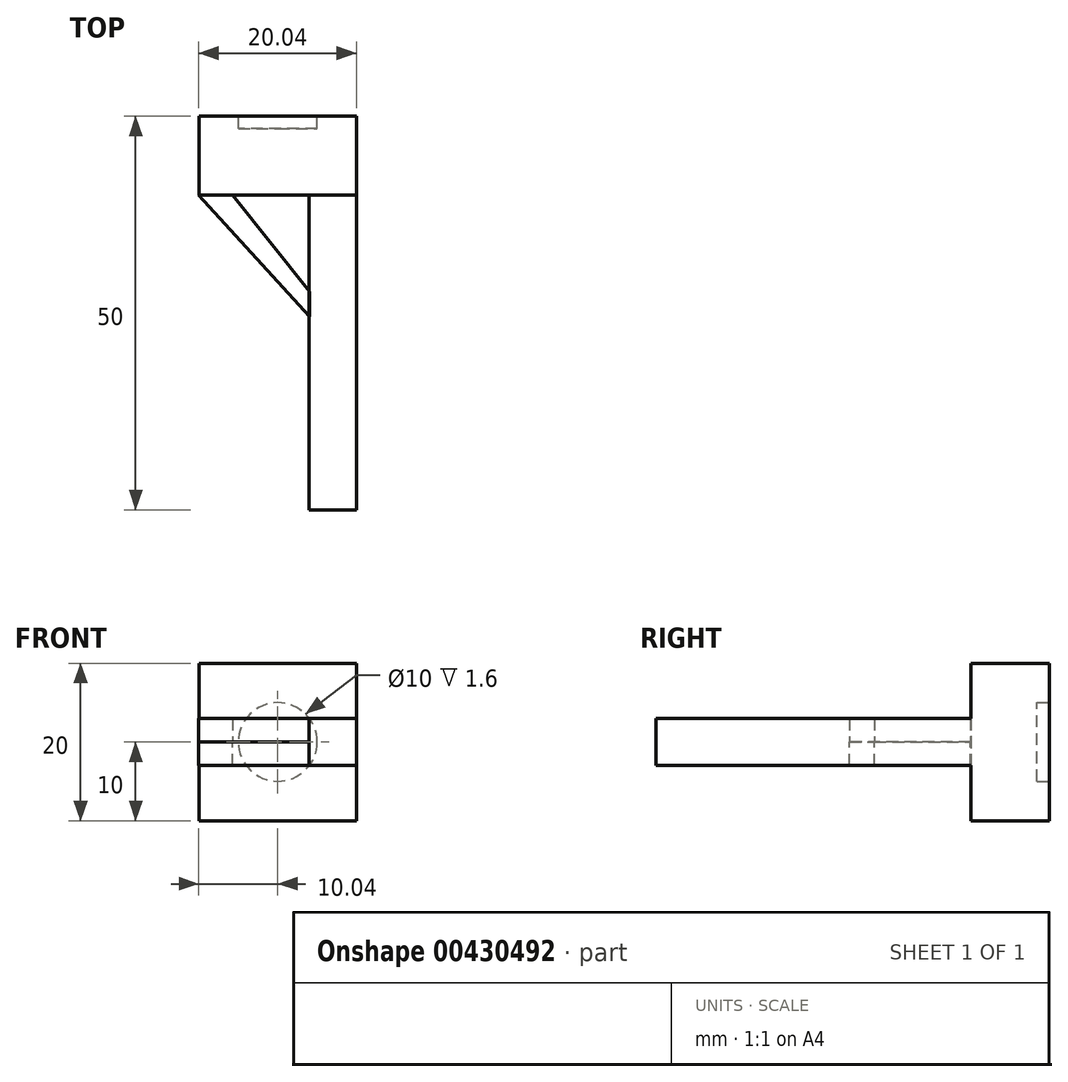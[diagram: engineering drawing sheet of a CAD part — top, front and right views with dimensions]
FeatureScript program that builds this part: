
annotation { "Feature Type Name" : "Feature", "Feature Type Description" : "" }
export const myFeature = defineFeature(function(context is Context, id is Id, definition is map)
    precondition{}
    {
        {
            var Q0;
            Q0=qCreatedBy(makeId("Front.planeOp"),FACE);
            var sketch = newSketch(context, id + "F0", { "sketchPlane" : qUnion([Q0])});
            skLineSegment(sketch, "E0.bottom", {"start": v(-10, 10) * mm, "end": v(10, 10) * mm});
            skLineSegment(sketch, "E0.top", {"start": v(-10, -10) * mm, "end": v(10, -10) * mm});
            skLineSegment(sketch, "E0.right", {"start": v(10, 10) * mm, "end": v(10, -10) * mm});
            skPoint(sketch, "E0.middle", {"position": v(0, 0) * mm});
            skLineSegment(sketch, "E1", {"start": v(-10, 10) * mm, "end": v(-10, -10) * mm});
            skSolve(sketch);
        }
        {
            var Q0;
            Q0=makeQuery(id+"F0.imprint","IMPRINT",FACE,{"disambiguationData":[TD([[makeQuery(id+"F0.imprint","IMPRINT",EDGE,{"derivedFrom":sQuery(id+"F0.wireOp",EDGE,"E0.bottom")}),-1.0]])]});
            extrude(context, id + "F1", {"entities" : qUnion([Q0]), "depth" : 10 * mm});
        }
        {
            var Q0;
            Q0=qCreatedBy(makeId("Front.planeOp"),FACE);
            var sketch = newSketch(context, id + "F2", { "sketchPlane" : qUnion([Q0])});
            skCircle(sketch, "E2", {"center": v(0, 0) * mm, "radius": 5 * mm});
            skSolve(sketch);
        }
        {
            var Q0;
            Q0 = qSketchRegion(id + "F2", true);
            extrude(context, id + "F3", {"entities" : qUnion([Q0]), "operationType" : NewBodyOperationType.REMOVE, "depth" : 1.6 * mm});
        }
        {
            var Q0;
            Q0=makeQuery(id+"F1.opExtrude","CAP_FACE",FACE,{"disambiguationData":[OSD([sQuery(id+"F0.wireOp",EDGE,"E0.bottom"),sQuery(id+"F0.wireOp",EDGE,"E0.top"),sQuery(id+"F0.wireOp",EDGE,"E0.right"),sQuery(id+"F0.wireOp",EDGE,"E1")])],"isStart":false});
            var sketch = newSketch(context, id + "F4", { "sketchPlane" : qUnion([Q0])});
            skLineSegment(sketch, "E3", {"start": v(10, 0) * mm, "end": v(10, 3) * mm});
            skLineSegment(sketch, "E4", {"start": v(10, 0) * mm, "end": v(10, -3) * mm});
            skLineSegment(sketch, "E5", {"start": v(10, 3) * mm, "end": v(4, 3) * mm});
            skLineSegment(sketch, "E6", {"start": v(4, 3) * mm, "end": v(4, -3) * mm});
            skLineSegment(sketch, "E7", {"start": v(4, -3) * mm, "end": v(10, -3) * mm});
            skSolve(sketch);
        }
        {
            var Q0;
            Q0 = qSketchRegion(id + "F4", true);
            extrude(context, id + "F5", {"entities" : qUnion([Q0]), "operationType" : NewBodyOperationType.ADD, "depth" : 40 * mm});
        }
        {
            var Q0;
            Q0=qCreatedBy(makeId("Top.planeOp"),FACE);
            var sketch = newSketch(context, id + "F6", { "sketchPlane" : qUnion([Q0])});
            skLineSegment(sketch, "E8", {"start": v(4.02, -22.26) * mm, "end": v(-5.72, -10.03) * mm});
            skLineSegment(sketch, "E9", {"start": v(-5.72, -10.03) * mm, "end": v(-10.04, -10.03) * mm});
            skLineSegment(sketch, "E10", {"start": v(-10.04, -10.03) * mm, "end": v(4.02, -25.42) * mm});
            skLineSegment(sketch, "E11", {"start": v(4.02, -25.42) * mm, "end": v(4.02, -22.26) * mm});
            skSolve(sketch);
        }
        {
            var Q0;
            Q0 = qSketchRegion(id + "F6", true);
            extrude(context, id + "F7", {"entities" : qUnion([Q0]), "depth" : 3 * mm});
        }
        {
            var Q0;
            Q0=makeQuery(id+"F7.opExtrude","CAP_FACE",FACE,{"disambiguationData":[OSD([sQuery(id+"F6.wireOp",EDGE,"E8"),sQuery(id+"F6.wireOp",EDGE,"E9"),sQuery(id+"F6.wireOp",EDGE,"E10"),sQuery(id+"F6.wireOp",EDGE,"E11")])],"isStart":true});
            extrude(context, id + "F8", {"entities" : qUnion([Q0]), "depth" : 3 * mm});
        }
    });
